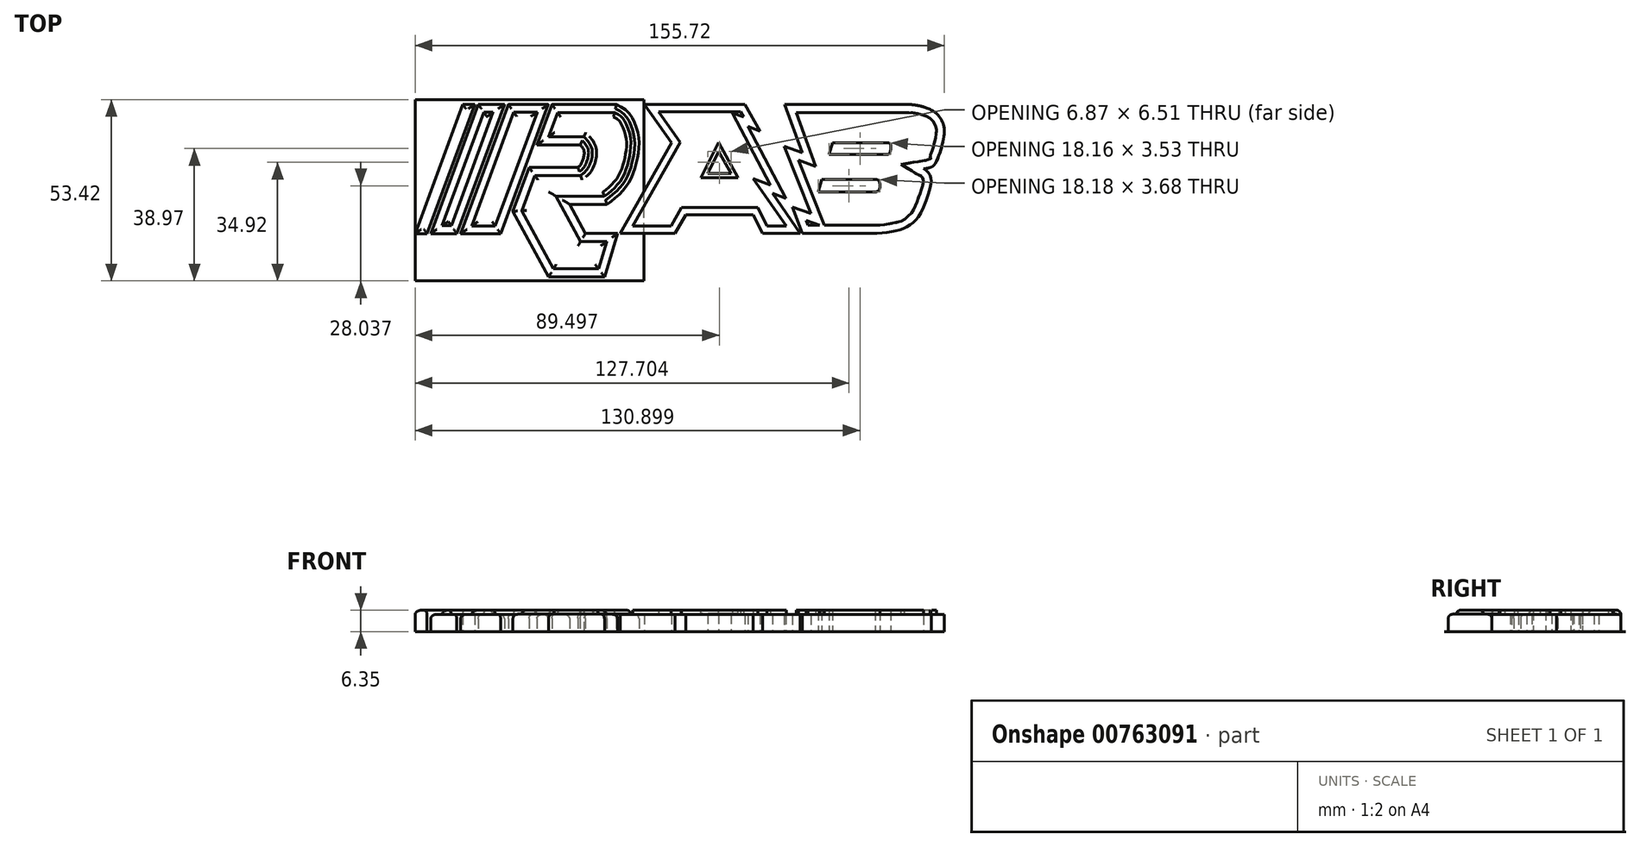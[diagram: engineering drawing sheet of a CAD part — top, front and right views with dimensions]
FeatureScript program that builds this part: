
annotation { "Feature Type Name" : "Feature", "Feature Type Description" : "" }
export const myFeature = defineFeature(function(context is Context, id is Id, definition is map)
    precondition{}
    {
        {
            var Q0;
            Q0=qCreatedBy(makeId("Top.planeOp"),FACE);
            var sketch = newSketch(context, id + "F0", { "sketchPlane" : qUnion([Q0])});
            skLineSegment(sketch, "E0", {"start": v(208.26, 38.07) * mm, "end": v(177.15, 38.07) * mm});
            skLineSegment(sketch, "E1", {"start": v(0, 0) * mm, "end": v(14, 38.07) * mm});
            skLineSegment(sketch, "E2", {"start": v(25.15, 0) * mm, "end": v(13.4, 0) * mm});
            skLineSegment(sketch, "E3", {"start": v(17.5, 38.07) * mm, "end": v(3.5, 0) * mm});
            skLineSegment(sketch, "E4", {"start": v(4.59, 0) * mm, "end": v(18.6, 38.07) * mm});
            skLineSegment(sketch, "E5", {"start": v(26.26, 38.07) * mm, "end": v(12.25, 0) * mm});
            skLineSegment(sketch, "E6", {"start": v(13.4, 0) * mm, "end": v(27.4, 38.07) * mm});
            skLineSegment(sketch, "E7", {"start": v(39.16, 38.07) * mm, "end": v(25.15, 0) * mm});
            skLineSegment(sketch, "E8", {"start": v(35.85, 26.18) * mm, "end": v(40.22, 38.07) * mm});
            skLineSegment(sketch, "E9", {"start": v(35.85, 26.18) * mm, "end": v(48.58, 26.18) * mm});
            skLineSegment(sketch, "E10", {"start": v(47.9, 19.52) * mm, "end": v(33.54, 19.52) * mm});
            skLineSegment(sketch, "E11", {"start": v(33.54, 19.52) * mm, "end": v(28.77, 6.57) * mm});
            skLineSegment(sketch, "E12", {"start": v(28.77, 6.57) * mm, "end": v(39.28, -12.73) * mm});
            skLineSegment(sketch, "E13", {"start": v(39.28, -12.73) * mm, "end": v(55.72, -12.73) * mm});
            skLineSegment(sketch, "E14", {"start": v(55.72, -12.73) * mm, "end": v(59.6, 0.09) * mm});
            skLineSegment(sketch, "E15", {"start": v(59.6, 0.09) * mm, "end": v(50.12, 0.09) * mm});
            skLineSegment(sketch, "E16", {"start": v(50.12, 0.09) * mm, "end": v(45.46, 8.65) * mm});
            skLineSegment(sketch, "E17", {"start": v(45.46, 8.65) * mm, "end": v(56.44, 8.65) * mm});
            skLineSegment(sketch, "E18", {"start": v(60.39, 0.09) * mm, "end": v(76.53, 0.09) * mm});
            skLineSegment(sketch, "E19", {"start": v(67.47, 38.07) * mm, "end": v(75.46, 26.74) * mm});
            skLineSegment(sketch, "E20", {"start": v(75.46, 26.74) * mm, "end": v(60.39, 0.09) * mm});
            skLineSegment(sketch, "E21", {"start": v(76.53, 0.09) * mm, "end": v(79.61, 5.54) * mm});
            skLineSegment(sketch, "E22", {"start": v(79.61, 5.54) * mm, "end": v(99.49, 5.54) * mm});
            skLineSegment(sketch, "E23", {"start": v(99.49, 5.54) * mm, "end": v(102.21, 0.09) * mm});
            skLineSegment(sketch, "E24", {"start": v(97.03, 38.07) * mm, "end": v(101.52, 30.22) * mm});
            skLineSegment(sketch, "E25", {"start": v(101.52, 30.22) * mm, "end": v(97.9, 31.58) * mm});
            skLineSegment(sketch, "E26", {"start": v(97.9, 31.58) * mm, "end": v(109.11, 10.42) * mm});
            skLineSegment(sketch, "E27", {"start": v(109.11, 10.42) * mm, "end": v(105.13, 11.87) * mm});
            skLineSegment(sketch, "E28", {"start": v(105.13, 11.87) * mm, "end": v(113.36, 0.09) * mm});
            skLineSegment(sketch, "E29", {"start": v(92.93, 17.75) * mm, "end": v(86.06, 17.75) * mm});
            skLineSegment(sketch, "E30", {"start": v(86.06, 17.75) * mm, "end": v(89.32, 24.25) * mm});
            skLineSegment(sketch, "E31", {"start": v(89.32, 24.25) * mm, "end": v(92.93, 17.75) * mm});
            skLineSegment(sketch, "E32", {"start": v(108.71, 38.07) * mm, "end": v(113.9, 23.8) * mm});
            skLineSegment(sketch, "E33", {"start": v(113.9, 23.8) * mm, "end": v(108.66, 25.8) * mm});
            skLineSegment(sketch, "E34", {"start": v(108.66, 25.8) * mm, "end": v(116.52, 5.9) * mm});
            skLineSegment(sketch, "E35", {"start": v(116.52, 5.9) * mm, "end": v(111, 7.9) * mm});
            skLineSegment(sketch, "E36", {"start": v(111, 7.9) * mm, "end": v(114, 0.09) * mm});
            skLineSegment(sketch, "E37", {"start": v(122.84, 26.81) * mm, "end": v(121.82, 23.29) * mm});
            skLineSegment(sketch, "E38", {"start": v(118.61, 12.28) * mm, "end": v(135.38, 12.28) * mm});
            skLineSegment(sketch, "E39", {"start": v(119.68, 15.96) * mm, "end": v(135.79, 15.96) * mm});
            skLineSegment(sketch, "E40", {"start": v(122.84, 26.81) * mm, "end": v(139.21, 26.81) * mm});
            skLineSegment(sketch, "E41", {"start": v(121.82, 23.29) * mm, "end": v(138.81, 23.29) * mm});
            skLineSegment(sketch, "E42", {"start": v(154.94, 38.07) * mm, "end": v(158.48, 30.05) * mm});
            skLineSegment(sketch, "E43", {"start": v(158.48, 30.05) * mm, "end": v(149.8, 0.09) * mm});
            skLineSegment(sketch, "E44", {"start": v(174.28, 38.07) * mm, "end": v(163.42, 0.09) * mm});
            skLineSegment(sketch, "E45", {"start": v(177.15, 38.07) * mm, "end": v(166.29, 0.09) * mm});
            skLineSegment(sketch, "E46", {"start": v(199.63, 25.83) * mm, "end": v(187.3, 25.83) * mm});
            skLineSegment(sketch, "E47", {"start": v(187.3, 25.83) * mm, "end": v(183.47, 12.44) * mm});
            skLineSegment(sketch, "E48", {"start": v(183.47, 12.44) * mm, "end": v(198.12, 12.44) * mm});
            skLineSegment(sketch, "E49", {"start": v(203.43, 21.85) * mm, "end": v(201.46, 14.99) * mm});
            skFitSpline(sketch, "E50", {"points": [v(219.55, 26.88) * mm, v(219.55, 31.52) * mm, v(217.56, 35.22) * mm, v(214.71, 36.84) * mm, v(208.26, 38.07) * mm], "startDerivative": vector(2.3, 18.78) * mm, "endDerivative": vector(-24.45, 0) * mm});
            skLineSegment(sketch, "E51", {"start": v(219.55, 26.88) * mm, "end": v(215.38, 11.32) * mm});
            skFitSpline(sketch, "E52", {"points": [v(149.65, 19.1) * mm, v(151.8, 19.57) * mm, v(153.28, 21.06) * mm, v(155.68, 29.22) * mm, v(155.1, 33.05) * mm, v(153.47, 35.33) * mm, v(150.12, 37.18) * mm, v(144.89, 38.07) * mm], "startDerivative": vector(20.2, 3.41) * mm, "endDerivative": vector(-28.09, 0) * mm});
            skFitSpline(sketch, "E53", {"points": [v(149.65, 19.1) * mm, v(151.02, 18) * mm, v(151.86, 16.02) * mm, v(151.72, 14.12) * mm, v(148.83, 6.08) * mm, v(146.58, 3.33) * mm, v(143.97, 1.57) * mm, v(140.72, 0.72) * mm, v(135.93, 0.09) * mm], "startDerivative": vector(16.43, -10.07) * mm, "endDerivative": vector(-33.98, 0) * mm});
            skFitSpline(sketch, "E54", {"points": [v(139.21, 26.81) * mm, v(139.63, 26.6) * mm, v(139.95, 26.07) * mm, v(139.77, 23.99) * mm, v(139.53, 23.54) * mm, v(138.81, 23.29) * mm], "startDerivative": vector(3.09, 0) * mm, "endDerivative": vector(-4.49, 0) * mm});
            skFitSpline(sketch, "E55", {"points": [v(135.79, 15.96) * mm, v(136.31, 15.73) * mm, v(136.7, 15.08) * mm, v(136.71, 13.28) * mm, v(136.38, 12.68) * mm, v(135.38, 12.28) * mm], "startDerivative": vector(3.73, 0) * mm, "endDerivative": vector(-8.7, -0.89) * mm});
            skFitSpline(sketch, "E56", {"points": [v(59.25, 38.07) * mm, v(62.12, 36.32) * mm, v(64.27, 33.3) * mm, v(65.78, 28.2) * mm, v(65.5, 22.76) * mm, v(63.84, 16.87) * mm, v(60.61, 12.07) * mm, v(56.44, 8.65) * mm], "startDerivative": vector(25.95, -13.02) * mm, "endDerivative": vector(-29.28, -21.25) * mm});
            skFitSpline(sketch, "E57", {"points": [v(199.63, 25.83) * mm, v(200.99, 25.52) * mm, v(202.05, 24.9) * mm, v(202.89, 23.96) * mm, v(203.43, 21.85) * mm], "startDerivative": vector(5.58, 0) * mm, "endDerivative": vector(-1.33, -10.82) * mm});
            skFitSpline(sketch, "E58", {"points": [v(198.12, 12.44) * mm, v(199.3, 12.72) * mm, v(200.4, 13.16) * mm, v(201.08, 13.97) * mm, v(201.46, 14.99) * mm], "startDerivative": vector(4.57, 1.01) * mm, "endDerivative": vector(1.33, 4.26) * mm});
            skLineSegment(sketch, "E59.trimOffspring", {"start": v(17.5, 38.07) * mm, "end": v(14, 38.07) * mm});
            skLineSegment(sketch, "E60.trimOffspring", {"start": v(26.26, 38.07) * mm, "end": v(18.6, 38.07) * mm});
            skLineSegment(sketch, "E61.trimOffspring", {"start": v(39.16, 38.07) * mm, "end": v(27.4, 38.07) * mm});
            skLineSegment(sketch, "E62.trimOffspring", {"start": v(59.25, 38.07) * mm, "end": v(40.22, 38.07) * mm});
            skLineSegment(sketch, "E63.trimOffspring", {"start": v(12.25, 0) * mm, "end": v(4.59, 0) * mm});
            skLineSegment(sketch, "E64.trimOffspring", {"start": v(3.5, 0) * mm, "end": v(0, 0) * mm});
            skLineSegment(sketch, "E65.trimOffspring", {"start": v(102.21, 0.09) * mm, "end": v(113.36, 0.09) * mm});
            skLineSegment(sketch, "E66.trimOffspring", {"start": v(114, 0.09) * mm, "end": v(135.93, 0.09) * mm});
            skLineSegment(sketch, "E67.trimOffspring", {"start": v(97.03, 38.07) * mm, "end": v(67.47, 38.07) * mm});
            skLineSegment(sketch, "E68.trimOffspring", {"start": v(119.68, 15.96) * mm, "end": v(118.61, 12.28) * mm});
            skLineSegment(sketch, "E69.trimOffspring", {"start": v(144.89, 38.07) * mm, "end": v(108.71, 38.07) * mm});
            skLineSegment(sketch, "E70.trimOffspring", {"start": v(149.8, 0.09) * mm, "end": v(163.42, 0.09) * mm});
            skLineSegment(sketch, "E71.trimOffspring", {"start": v(166.29, 0.09) * mm, "end": v(197.11, 0.09) * mm});
            skLineSegment(sketch, "E72.trimOffspring", {"start": v(174.28, 38.07) * mm, "end": v(154.94, 38.07) * mm});
            skFitSpline(sketch, "E73", {"points": [v(215.38, 11.32) * mm, v(214.17, 8.68) * mm, v(212.23, 5.94) * mm, v(209.39, 3.57) * mm, v(206.3, 1.9) * mm, v(202.66, 0.86) * mm, v(197.11, 0.09) * mm], "startDerivative": vector(-7.47, -18.05) * mm, "endDerivative": vector(-28.9, 0) * mm});
            skFitSpline(sketch, "E74", {"points": [v(48.58, 26.18) * mm, v(49.62, 24.65) * mm, v(49.56, 22.47) * mm, v(48.58, 20.18) * mm, v(47.9, 19.52) * mm], "startDerivative": vector(5.02, -5.67) * mm, "endDerivative": vector(-3.78, -2.78) * mm});
            skSolve(sketch);
        }
        {
            var Q0;
            Q0=makeQuery(id+"F0.imprint","IMPRINT",FACE,{"disambiguationData":[TD([[makeQuery(id+"F0.imprint","IMPRINT",EDGE,{"derivedFrom":sQuery(id+"F0.wireOp",EDGE,"E8")}),-1.0]])]});
            var Q1;
            Q1=makeQuery(id+"F0.imprint","IMPRINT",FACE,{"disambiguationData":[TD([[makeQuery(id+"F0.imprint","IMPRINT",EDGE,{"derivedFrom":sQuery(id+"F0.wireOp",EDGE,"E2")}),-1.0]])]});
            var Q2;
            Q2=makeQuery(id+"F0.imprint","IMPRINT",FACE,{"disambiguationData":[TD([[makeQuery(id+"F0.imprint","IMPRINT",EDGE,{"derivedFrom":sQuery(id+"F0.wireOp",EDGE,"E4")}),-1.0]])]});
            var Q3;
            Q3=makeQuery(id+"F0.imprint","IMPRINT",FACE,{"disambiguationData":[TD([[makeQuery(id+"F0.imprint","IMPRINT",EDGE,{"derivedFrom":sQuery(id+"F0.wireOp",EDGE,"E1")}),-1.0]])]});
            extrude(context, id + "F1", {"entities" : qUnion([Q0, Q1, Q2, Q3]), "depth" : 6.35 * mm, "offsetDistance" : 25.4 * mm});
        }
        {
            var Q0;
            Q0=qCreatedBy(makeId("Front.planeOp"),FACE);
            cPlane(context, id + "F2", {"entities" : qUnion([Q0]), "cplaneType" : CPlaneType.OFFSET, "offset" : 25.4 * mm, "oppositeDirection" : true, "width" : 152.4 * mm, "height" : 152.4 * mm});
        }
        {
            var Q0;
            Q0=qCreatedBy(id+"F2.planeOp",FACE);
            var sketch = newSketch(context, id + "F3", { "sketchPlane" : qUnion([Q0])});
            skLineSegment(sketch, "E75", {"start": v(63.44, 6.43) * mm, "end": v(63.44, 5.16) * mm});
            skLineSegment(sketch, "E76", {"start": v(63.44, 5.16) * mm, "end": v(65.98, 5.16) * mm});
            skLineSegment(sketch, "E77", {"start": v(65.98, 5.16) * mm, "end": v(65.98, 6.43) * mm});
            skLineSegment(sketch, "E78", {"start": v(65.98, 6.43) * mm, "end": v(63.44, 6.43) * mm});
            skSolve(sketch);
        }
        {
            var Q0;
            Q0=qSketchRegion(id+"F3",true);
            var Q1;
            Q1=makeQuery(id+"F1.opExtrude","CAP_EDGE",EDGE,{"disambiguationData":[OSD([sQuery(id+"F0.wireOp",EDGE,"E56")])],"isStart":false});
            var Q2;
            Q2=makeQuery(id+"F1.opExtrude","CAP_EDGE",EDGE,{"disambiguationData":[OSD([sQuery(id+"F0.wireOp",EDGE,"E17")])],"isStart":false});
            var Q3;
            Q3=makeQuery(id+"F1.opExtrude","CAP_EDGE",EDGE,{"disambiguationData":[OSD([sQuery(id+"F0.wireOp",EDGE,"E16")])],"isStart":false});
            var Q4;
            Q4=makeQuery(id+"F1.opExtrude","CAP_EDGE",EDGE,{"disambiguationData":[OSD([sQuery(id+"F0.wireOp",EDGE,"E15")])],"isStart":false});
            var Q5;
            Q5=makeQuery(id+"F1.opExtrude","CAP_EDGE",EDGE,{"disambiguationData":[OSD([sQuery(id+"F0.wireOp",EDGE,"E14")])],"isStart":false});
            var Q6;
            Q6=makeQuery(id+"F1.opExtrude","CAP_EDGE",EDGE,{"disambiguationData":[OSD([sQuery(id+"F0.wireOp",EDGE,"E13")])],"isStart":false});
            var Q7;
            Q7=makeQuery(id+"F1.opExtrude","CAP_EDGE",EDGE,{"disambiguationData":[OSD([sQuery(id+"F0.wireOp",EDGE,"E12")])],"isStart":false});
            var Q8;
            Q8=makeQuery(id+"F1.opExtrude","CAP_EDGE",EDGE,{"disambiguationData":[OSD([sQuery(id+"F0.wireOp",EDGE,"E11")])],"isStart":false});
            var Q9;
            Q9=makeQuery(id+"F1.opExtrude","CAP_EDGE",EDGE,{"disambiguationData":[OSD([sQuery(id+"F0.wireOp",EDGE,"E10")])],"isStart":false});
            var Q10;
            Q10=makeQuery(id+"F1.opExtrude","CAP_EDGE",EDGE,{"disambiguationData":[OSD([sQuery(id+"F0.wireOp",EDGE,"E74")])],"isStart":false});
            var Q11;
            Q11=makeQuery(id+"F1.opExtrude","CAP_EDGE",EDGE,{"disambiguationData":[OSD([sQuery(id+"F0.wireOp",EDGE,"E9")])],"isStart":false});
            var Q12;
            Q12=makeQuery(id+"F1.opExtrude","CAP_EDGE",EDGE,{"disambiguationData":[OSD([sQuery(id+"F0.wireOp",EDGE,"E8")])],"isStart":false});
            var Q13;
            Q13=makeQuery(id+"F1.opExtrude","CAP_EDGE",EDGE,{"disambiguationData":[OSD([sQuery(id+"F0.wireOp",EDGE,"E62.trimOffspring")])],"isStart":false});
            sweep(context, id + "F4", {"operationType" : NewBodyOperationType.REMOVE, "profiles" : qUnion([Q0]), "path" : qUnion([Q1, Q2, Q3, Q4, Q5, Q6, Q7, Q8, Q9, Q10, Q11, Q12, Q13])});
        }
        {
            var Q0;
            Q0=qCreatedBy(id+"F2.planeOp",FACE);
            var sketch = newSketch(context, id + "F5", { "sketchPlane" : qUnion([Q0])});
            skLineSegment(sketch, "E79", {"start": v(32.09, 6.42) * mm, "end": v(32.09, 5.16) * mm});
            skLineSegment(sketch, "E80", {"start": v(32.09, 5.16) * mm, "end": v(34.63, 5.16) * mm});
            skLineSegment(sketch, "E81", {"start": v(34.63, 5.16) * mm, "end": v(34.63, 6.42) * mm});
            skLineSegment(sketch, "E82", {"start": v(34.63, 6.42) * mm, "end": v(32.09, 6.42) * mm});
            skSolve(sketch);
        }
        {
            var Q0;
            Q0=qSketchRegion(id+"F5",true);
            var Q1;
            Q1=makeQuery(id+"F1.opExtrude","CAP_EDGE",EDGE,{"disambiguationData":[OSD([sQuery(id+"F0.wireOp",EDGE,"E7")])],"isStart":false});
            var Q2;
            Q2=makeQuery(id+"F1.opExtrude","CAP_EDGE",EDGE,{"disambiguationData":[OSD([sQuery(id+"F0.wireOp",EDGE,"E2")])],"isStart":false});
            var Q3;
            Q3=makeQuery(id+"F1.opExtrude","CAP_EDGE",EDGE,{"disambiguationData":[OSD([sQuery(id+"F0.wireOp",EDGE,"E6")])],"isStart":false});
            var Q4;
            Q4=makeQuery(id+"F1.opExtrude","CAP_EDGE",EDGE,{"disambiguationData":[OSD([sQuery(id+"F0.wireOp",EDGE,"E61.trimOffspring")])],"isStart":false});
            sweep(context, id + "F6", {"operationType" : NewBodyOperationType.REMOVE, "profiles" : qUnion([Q0]), "path" : qUnion([Q1, Q2, Q3, Q4])});
        }
        {
            var Q0;
            Q0=qCreatedBy(id+"F2.planeOp",FACE);
            var sketch = newSketch(context, id + "F7", { "sketchPlane" : qUnion([Q0])});
            skLineSegment(sketch, "E83", {"start": v(19.13, 6.42) * mm, "end": v(19.13, 5.16) * mm});
            skLineSegment(sketch, "E84", {"start": v(19.13, 5.16) * mm, "end": v(21.67, 5.16) * mm});
            skLineSegment(sketch, "E85", {"start": v(21.67, 5.16) * mm, "end": v(21.67, 6.42) * mm});
            skLineSegment(sketch, "E86", {"start": v(21.67, 6.42) * mm, "end": v(19.13, 6.42) * mm});
            skSolve(sketch);
        }
        {
            var Q0;
            Q0=qSketchRegion(id+"F7",true);
            var Q1;
            Q1=makeQuery(id+"F1.opExtrude","CAP_EDGE",EDGE,{"disambiguationData":[OSD([sQuery(id+"F0.wireOp",EDGE,"E5")])],"isStart":false});
            var Q2;
            Q2=makeQuery(id+"F1.opExtrude","CAP_EDGE",EDGE,{"disambiguationData":[OSD([sQuery(id+"F0.wireOp",EDGE,"E63.trimOffspring")])],"isStart":false});
            var Q3;
            Q3=makeQuery(id+"F1.opExtrude","CAP_EDGE",EDGE,{"disambiguationData":[OSD([sQuery(id+"F0.wireOp",EDGE,"E4")])],"isStart":false});
            var Q4;
            Q4=makeQuery(id+"F1.opExtrude","CAP_EDGE",EDGE,{"disambiguationData":[OSD([sQuery(id+"F0.wireOp",EDGE,"E60.trimOffspring")])],"isStart":false});
            sweep(context, id + "F8", {"operationType" : NewBodyOperationType.REMOVE, "profiles" : qUnion([Q0]), "path" : qUnion([Q1, Q2, Q3, Q4])});
        }
        {
            var Q0;
            {var subQ0=sQuery(id+"F0.wireOp",EDGE,"E56");Q0=makeQuery(id+"F4.boolean.opBoolean","INTERSECT",EDGE,{"derivedFrom":[makeQuery(id+"F1.opExtrude","CAP_FACE",FACE,{"disambiguationData":[OSD([sQuery(id+"F0.wireOp",EDGE,"E8"),sQuery(id+"F0.wireOp",EDGE,"E9"),sQuery(id+"F0.wireOp",EDGE,"E10"),sQuery(id+"F0.wireOp",EDGE,"E11"),sQuery(id+"F0.wireOp",EDGE,"E12"),sQuery(id+"F0.wireOp",EDGE,"E13"),sQuery(id+"F0.wireOp",EDGE,"E14"),sQuery(id+"F0.wireOp",EDGE,"E15"),sQuery(id+"F0.wireOp",EDGE,"E16"),sQuery(id+"F0.wireOp",EDGE,"E17"),subQ0,sQuery(id+"F0.wireOp",EDGE,"E62.trimOffspring"),sQuery(id+"F0.wireOp",EDGE,"E74")])],"isStart":false}),makeQuery(id+"F4.opSweep","SWEPT_FACE",FACE,{"disambiguationData":[OSD([subQ0,sQuery(id+"F3.wireOp",EDGE,"E75")])]})]});}
            var Q1;
            {var subQ0=sQuery(id+"F0.wireOp",EDGE,"E17");Q1=makeQuery(id+"F4.boolean.opBoolean","INTERSECT",EDGE,{"derivedFrom":[makeQuery(id+"F1.opExtrude","CAP_FACE",FACE,{"disambiguationData":[OSD([sQuery(id+"F0.wireOp",EDGE,"E8"),sQuery(id+"F0.wireOp",EDGE,"E9"),sQuery(id+"F0.wireOp",EDGE,"E10"),sQuery(id+"F0.wireOp",EDGE,"E11"),sQuery(id+"F0.wireOp",EDGE,"E12"),sQuery(id+"F0.wireOp",EDGE,"E13"),sQuery(id+"F0.wireOp",EDGE,"E14"),sQuery(id+"F0.wireOp",EDGE,"E15"),sQuery(id+"F0.wireOp",EDGE,"E16"),subQ0,sQuery(id+"F0.wireOp",EDGE,"E56"),sQuery(id+"F0.wireOp",EDGE,"E62.trimOffspring"),sQuery(id+"F0.wireOp",EDGE,"E74")])],"isStart":false}),makeQuery(id+"F4.opSweep","SWEPT_FACE",FACE,{"disambiguationData":[OSD([subQ0,sQuery(id+"F3.wireOp",EDGE,"E75")])]})]});}
            var Q2;
            {var subQ0=sQuery(id+"F0.wireOp",EDGE,"E16");Q2=makeQuery(id+"F4.boolean.opBoolean","INTERSECT",EDGE,{"derivedFrom":[makeQuery(id+"F1.opExtrude","CAP_FACE",FACE,{"disambiguationData":[OSD([sQuery(id+"F0.wireOp",EDGE,"E8"),sQuery(id+"F0.wireOp",EDGE,"E9"),sQuery(id+"F0.wireOp",EDGE,"E10"),sQuery(id+"F0.wireOp",EDGE,"E11"),sQuery(id+"F0.wireOp",EDGE,"E12"),sQuery(id+"F0.wireOp",EDGE,"E13"),sQuery(id+"F0.wireOp",EDGE,"E14"),sQuery(id+"F0.wireOp",EDGE,"E15"),subQ0,sQuery(id+"F0.wireOp",EDGE,"E17"),sQuery(id+"F0.wireOp",EDGE,"E56"),sQuery(id+"F0.wireOp",EDGE,"E62.trimOffspring"),sQuery(id+"F0.wireOp",EDGE,"E74")])],"isStart":false}),makeQuery(id+"F4.opSweep","SWEPT_FACE",FACE,{"disambiguationData":[OSD([subQ0,sQuery(id+"F3.wireOp",EDGE,"E75")])]})]});}
            var Q3;
            {var subQ0=sQuery(id+"F0.wireOp",EDGE,"E15");Q3=makeQuery(id+"F4.boolean.opBoolean","INTERSECT",EDGE,{"derivedFrom":[makeQuery(id+"F1.opExtrude","CAP_FACE",FACE,{"disambiguationData":[OSD([sQuery(id+"F0.wireOp",EDGE,"E8"),sQuery(id+"F0.wireOp",EDGE,"E9"),sQuery(id+"F0.wireOp",EDGE,"E10"),sQuery(id+"F0.wireOp",EDGE,"E11"),sQuery(id+"F0.wireOp",EDGE,"E12"),sQuery(id+"F0.wireOp",EDGE,"E13"),sQuery(id+"F0.wireOp",EDGE,"E14"),subQ0,sQuery(id+"F0.wireOp",EDGE,"E16"),sQuery(id+"F0.wireOp",EDGE,"E17"),sQuery(id+"F0.wireOp",EDGE,"E56"),sQuery(id+"F0.wireOp",EDGE,"E62.trimOffspring"),sQuery(id+"F0.wireOp",EDGE,"E74")])],"isStart":false}),makeQuery(id+"F4.opSweep","SWEPT_FACE",FACE,{"disambiguationData":[OSD([subQ0,sQuery(id+"F3.wireOp",EDGE,"E75")])]})]});}
            var Q4;
            {var subQ0=sQuery(id+"F0.wireOp",EDGE,"E14");Q4=makeQuery(id+"F4.boolean.opBoolean","INTERSECT",EDGE,{"derivedFrom":[makeQuery(id+"F1.opExtrude","CAP_FACE",FACE,{"disambiguationData":[OSD([sQuery(id+"F0.wireOp",EDGE,"E8"),sQuery(id+"F0.wireOp",EDGE,"E9"),sQuery(id+"F0.wireOp",EDGE,"E10"),sQuery(id+"F0.wireOp",EDGE,"E11"),sQuery(id+"F0.wireOp",EDGE,"E12"),sQuery(id+"F0.wireOp",EDGE,"E13"),subQ0,sQuery(id+"F0.wireOp",EDGE,"E15"),sQuery(id+"F0.wireOp",EDGE,"E16"),sQuery(id+"F0.wireOp",EDGE,"E17"),sQuery(id+"F0.wireOp",EDGE,"E56"),sQuery(id+"F0.wireOp",EDGE,"E62.trimOffspring"),sQuery(id+"F0.wireOp",EDGE,"E74")])],"isStart":false}),makeQuery(id+"F4.opSweep","SWEPT_FACE",FACE,{"disambiguationData":[OSD([subQ0,sQuery(id+"F3.wireOp",EDGE,"E75")])]})]});}
            var Q5;
            Q5=makeQuery(id+"F4.boolean.opBoolean","INTERSECT",EDGE,{"derivedFrom":[makeQuery(id+"F1.opExtrude","SWEPT_FACE",FACE,{"disambiguationData":[OSD([sQuery(id+"F0.wireOp",EDGE,"E13")])]}),makeQuery(id+"F4.opSweep","SWEPT_FACE",FACE,{"disambiguationData":[OSD([sQuery(id+"F0.wireOp",EDGE,"E17"),sQuery(id+"F3.wireOp",EDGE,"E76")])]})]});
            var Q6;
            Q6=makeQuery(id+"F4.boolean.opBoolean","INTERSECT",EDGE,{"derivedFrom":[makeQuery(id+"F1.opExtrude","SWEPT_FACE",FACE,{"disambiguationData":[OSD([sQuery(id+"F0.wireOp",EDGE,"E14")])]}),makeQuery(id+"F4.opSweep","SWEPT_FACE",FACE,{"disambiguationData":[OSD([sQuery(id+"F0.wireOp",EDGE,"E17"),sQuery(id+"F3.wireOp",EDGE,"E76")])]})]});
            var Q7;
            {var subQ0=sQuery(id+"F0.wireOp",EDGE,"E17");Q7=makeQuery(id+"F4.boolean.opBoolean","INTERSECT",EDGE,{"derivedFrom":[makeQuery(id+"F1.opExtrude","SWEPT_FACE",FACE,{"disambiguationData":[OSD([subQ0])]}),makeQuery(id+"F4.opSweep","SWEPT_FACE",FACE,{"disambiguationData":[OSD([subQ0,sQuery(id+"F3.wireOp",EDGE,"E76")])]})]});}
            var Q8;
            Q8=makeQuery(id+"F4.boolean.opBoolean","INTERSECT",EDGE,{"derivedFrom":[makeQuery(id+"F1.opExtrude","SWEPT_FACE",FACE,{"disambiguationData":[OSD([sQuery(id+"F0.wireOp",EDGE,"E16")])]}),makeQuery(id+"F4.opSweep","SWEPT_FACE",FACE,{"disambiguationData":[OSD([sQuery(id+"F0.wireOp",EDGE,"E17"),sQuery(id+"F3.wireOp",EDGE,"E76")])]})]});
            var Q9;
            Q9=makeQuery(id+"F4.boolean.opBoolean","INTERSECT",EDGE,{"derivedFrom":[makeQuery(id+"F1.opExtrude","SWEPT_FACE",FACE,{"disambiguationData":[OSD([sQuery(id+"F0.wireOp",EDGE,"E15")])]}),makeQuery(id+"F4.opSweep","SWEPT_FACE",FACE,{"disambiguationData":[OSD([sQuery(id+"F0.wireOp",EDGE,"E17"),sQuery(id+"F3.wireOp",EDGE,"E76")])]})]});
            var Q10;
            Q10=makeQuery(id+"F4.boolean.opBoolean","INTERSECT",EDGE,{"derivedFrom":[makeQuery(id+"F1.opExtrude","SWEPT_FACE",FACE,{"disambiguationData":[OSD([sQuery(id+"F0.wireOp",EDGE,"E56")])]}),makeQuery(id+"F4.opSweep","SWEPT_FACE",FACE,{"disambiguationData":[OSD([sQuery(id+"F0.wireOp",EDGE,"E17"),sQuery(id+"F3.wireOp",EDGE,"E76")])]})]});
            var Q11;
            {var subQ0=sQuery(id+"F0.wireOp",EDGE,"E13");Q11=makeQuery(id+"F4.boolean.opBoolean","INTERSECT",EDGE,{"derivedFrom":[makeQuery(id+"F1.opExtrude","CAP_FACE",FACE,{"disambiguationData":[OSD([sQuery(id+"F0.wireOp",EDGE,"E8"),sQuery(id+"F0.wireOp",EDGE,"E9"),sQuery(id+"F0.wireOp",EDGE,"E10"),sQuery(id+"F0.wireOp",EDGE,"E11"),sQuery(id+"F0.wireOp",EDGE,"E12"),subQ0,sQuery(id+"F0.wireOp",EDGE,"E14"),sQuery(id+"F0.wireOp",EDGE,"E15"),sQuery(id+"F0.wireOp",EDGE,"E16"),sQuery(id+"F0.wireOp",EDGE,"E17"),sQuery(id+"F0.wireOp",EDGE,"E56"),sQuery(id+"F0.wireOp",EDGE,"E62.trimOffspring"),sQuery(id+"F0.wireOp",EDGE,"E74")])],"isStart":false}),makeQuery(id+"F4.opSweep","SWEPT_FACE",FACE,{"disambiguationData":[OSD([subQ0,sQuery(id+"F3.wireOp",EDGE,"E75")])]})]});}
            var Q12;
            {var subQ0=sQuery(id+"F0.wireOp",EDGE,"E12");Q12=makeQuery(id+"F4.boolean.opBoolean","INTERSECT",EDGE,{"derivedFrom":[makeQuery(id+"F1.opExtrude","CAP_FACE",FACE,{"disambiguationData":[OSD([sQuery(id+"F0.wireOp",EDGE,"E8"),sQuery(id+"F0.wireOp",EDGE,"E9"),sQuery(id+"F0.wireOp",EDGE,"E10"),sQuery(id+"F0.wireOp",EDGE,"E11"),subQ0,sQuery(id+"F0.wireOp",EDGE,"E13"),sQuery(id+"F0.wireOp",EDGE,"E14"),sQuery(id+"F0.wireOp",EDGE,"E15"),sQuery(id+"F0.wireOp",EDGE,"E16"),sQuery(id+"F0.wireOp",EDGE,"E17"),sQuery(id+"F0.wireOp",EDGE,"E56"),sQuery(id+"F0.wireOp",EDGE,"E62.trimOffspring"),sQuery(id+"F0.wireOp",EDGE,"E74")])],"isStart":false}),makeQuery(id+"F4.opSweep","SWEPT_FACE",FACE,{"disambiguationData":[OSD([subQ0,sQuery(id+"F3.wireOp",EDGE,"E75")])]})]});}
            var Q13;
            Q13=makeQuery(id+"F4.boolean.opBoolean","INTERSECT",EDGE,{"derivedFrom":[makeQuery(id+"F1.opExtrude","SWEPT_FACE",FACE,{"disambiguationData":[OSD([sQuery(id+"F0.wireOp",EDGE,"E12")])]}),makeQuery(id+"F4.opSweep","SWEPT_FACE",FACE,{"disambiguationData":[OSD([sQuery(id+"F0.wireOp",EDGE,"E17"),sQuery(id+"F3.wireOp",EDGE,"E76")])]})]});
            var Q14;
            Q14=makeQuery(id+"F4.boolean.opBoolean","INTERSECT",EDGE,{"derivedFrom":[makeQuery(id+"F1.opExtrude","SWEPT_FACE",FACE,{"disambiguationData":[OSD([sQuery(id+"F0.wireOp",EDGE,"E11")])]}),makeQuery(id+"F4.opSweep","SWEPT_FACE",FACE,{"disambiguationData":[OSD([sQuery(id+"F0.wireOp",EDGE,"E17"),sQuery(id+"F3.wireOp",EDGE,"E76")])]})]});
            var Q15;
            Q15=makeQuery(id+"F4.boolean.opBoolean","INTERSECT",EDGE,{"derivedFrom":[makeQuery(id+"F1.opExtrude","SWEPT_FACE",FACE,{"disambiguationData":[OSD([sQuery(id+"F0.wireOp",EDGE,"E10")])]}),makeQuery(id+"F4.opSweep","SWEPT_FACE",FACE,{"disambiguationData":[OSD([sQuery(id+"F0.wireOp",EDGE,"E17"),sQuery(id+"F3.wireOp",EDGE,"E76")])]})]});
            var Q16;
            {var subQ0=sQuery(id+"F0.wireOp",EDGE,"E11");Q16=makeQuery(id+"F4.boolean.opBoolean","INTERSECT",EDGE,{"derivedFrom":[makeQuery(id+"F1.opExtrude","CAP_FACE",FACE,{"disambiguationData":[OSD([sQuery(id+"F0.wireOp",EDGE,"E8"),sQuery(id+"F0.wireOp",EDGE,"E9"),sQuery(id+"F0.wireOp",EDGE,"E10"),subQ0,sQuery(id+"F0.wireOp",EDGE,"E12"),sQuery(id+"F0.wireOp",EDGE,"E13"),sQuery(id+"F0.wireOp",EDGE,"E14"),sQuery(id+"F0.wireOp",EDGE,"E15"),sQuery(id+"F0.wireOp",EDGE,"E16"),sQuery(id+"F0.wireOp",EDGE,"E17"),sQuery(id+"F0.wireOp",EDGE,"E56"),sQuery(id+"F0.wireOp",EDGE,"E62.trimOffspring"),sQuery(id+"F0.wireOp",EDGE,"E74")])],"isStart":false}),makeQuery(id+"F4.opSweep","SWEPT_FACE",FACE,{"disambiguationData":[OSD([subQ0,sQuery(id+"F3.wireOp",EDGE,"E75")])]})]});}
            var Q17;
            {var subQ0=sQuery(id+"F0.wireOp",EDGE,"E10");Q17=makeQuery(id+"F4.boolean.opBoolean","INTERSECT",EDGE,{"derivedFrom":[makeQuery(id+"F1.opExtrude","CAP_FACE",FACE,{"disambiguationData":[OSD([sQuery(id+"F0.wireOp",EDGE,"E8"),sQuery(id+"F0.wireOp",EDGE,"E9"),subQ0,sQuery(id+"F0.wireOp",EDGE,"E11"),sQuery(id+"F0.wireOp",EDGE,"E12"),sQuery(id+"F0.wireOp",EDGE,"E13"),sQuery(id+"F0.wireOp",EDGE,"E14"),sQuery(id+"F0.wireOp",EDGE,"E15"),sQuery(id+"F0.wireOp",EDGE,"E16"),sQuery(id+"F0.wireOp",EDGE,"E17"),sQuery(id+"F0.wireOp",EDGE,"E56"),sQuery(id+"F0.wireOp",EDGE,"E62.trimOffspring"),sQuery(id+"F0.wireOp",EDGE,"E74")])],"isStart":false}),makeQuery(id+"F4.opSweep","SWEPT_FACE",FACE,{"disambiguationData":[OSD([subQ0,sQuery(id+"F3.wireOp",EDGE,"E75")])]})]});}
            var Q18;
            Q18=makeQuery(id+"F4.boolean.opBoolean","INTERSECT",EDGE,{"derivedFrom":[makeQuery(id+"F1.opExtrude","SWEPT_FACE",FACE,{"disambiguationData":[OSD([sQuery(id+"F0.wireOp",EDGE,"E74")])]}),makeQuery(id+"F4.opSweep","SWEPT_FACE",FACE,{"disambiguationData":[OSD([sQuery(id+"F0.wireOp",EDGE,"E17"),sQuery(id+"F3.wireOp",EDGE,"E76")])]})]});
            var Q19;
            {var subQ0=sQuery(id+"F0.wireOp",EDGE,"E74");Q19=makeQuery(id+"F4.boolean.opBoolean","INTERSECT",EDGE,{"derivedFrom":[makeQuery(id+"F1.opExtrude","CAP_FACE",FACE,{"disambiguationData":[OSD([sQuery(id+"F0.wireOp",EDGE,"E8"),sQuery(id+"F0.wireOp",EDGE,"E9"),sQuery(id+"F0.wireOp",EDGE,"E10"),sQuery(id+"F0.wireOp",EDGE,"E11"),sQuery(id+"F0.wireOp",EDGE,"E12"),sQuery(id+"F0.wireOp",EDGE,"E13"),sQuery(id+"F0.wireOp",EDGE,"E14"),sQuery(id+"F0.wireOp",EDGE,"E15"),sQuery(id+"F0.wireOp",EDGE,"E16"),sQuery(id+"F0.wireOp",EDGE,"E17"),sQuery(id+"F0.wireOp",EDGE,"E56"),sQuery(id+"F0.wireOp",EDGE,"E62.trimOffspring"),subQ0])],"isStart":false}),makeQuery(id+"F4.opSweep","SWEPT_FACE",FACE,{"disambiguationData":[OSD([subQ0,sQuery(id+"F3.wireOp",EDGE,"E75")])]})]});}
            var Q20;
            {var subQ0=sQuery(id+"F0.wireOp",EDGE,"E9");Q20=makeQuery(id+"F4.boolean.opBoolean","INTERSECT",EDGE,{"derivedFrom":[makeQuery(id+"F1.opExtrude","CAP_FACE",FACE,{"disambiguationData":[OSD([sQuery(id+"F0.wireOp",EDGE,"E8"),subQ0,sQuery(id+"F0.wireOp",EDGE,"E10"),sQuery(id+"F0.wireOp",EDGE,"E11"),sQuery(id+"F0.wireOp",EDGE,"E12"),sQuery(id+"F0.wireOp",EDGE,"E13"),sQuery(id+"F0.wireOp",EDGE,"E14"),sQuery(id+"F0.wireOp",EDGE,"E15"),sQuery(id+"F0.wireOp",EDGE,"E16"),sQuery(id+"F0.wireOp",EDGE,"E17"),sQuery(id+"F0.wireOp",EDGE,"E56"),sQuery(id+"F0.wireOp",EDGE,"E62.trimOffspring"),sQuery(id+"F0.wireOp",EDGE,"E74")])],"isStart":false}),makeQuery(id+"F4.opSweep","SWEPT_FACE",FACE,{"disambiguationData":[OSD([subQ0,sQuery(id+"F3.wireOp",EDGE,"E75")])]})]});}
            var Q21;
            Q21=makeQuery(id+"F4.boolean.opBoolean","INTERSECT",EDGE,{"derivedFrom":[makeQuery(id+"F1.opExtrude","SWEPT_FACE",FACE,{"disambiguationData":[OSD([sQuery(id+"F0.wireOp",EDGE,"E9")])]}),makeQuery(id+"F4.opSweep","SWEPT_FACE",FACE,{"disambiguationData":[OSD([sQuery(id+"F0.wireOp",EDGE,"E17"),sQuery(id+"F3.wireOp",EDGE,"E76")])]})]});
            var Q22;
            Q22=makeQuery(id+"F4.boolean.opBoolean","INTERSECT",EDGE,{"derivedFrom":[makeQuery(id+"F1.opExtrude","SWEPT_FACE",FACE,{"disambiguationData":[OSD([sQuery(id+"F0.wireOp",EDGE,"E8")])]}),makeQuery(id+"F4.opSweep","SWEPT_FACE",FACE,{"disambiguationData":[OSD([sQuery(id+"F0.wireOp",EDGE,"E17"),sQuery(id+"F3.wireOp",EDGE,"E76")])]})]});
            var Q23;
            {var subQ0=sQuery(id+"F0.wireOp",EDGE,"E62.trimOffspring");Q23=makeQuery(id+"F4.boolean.opBoolean","INTERSECT",EDGE,{"derivedFrom":[makeQuery(id+"F1.opExtrude","CAP_FACE",FACE,{"disambiguationData":[OSD([sQuery(id+"F0.wireOp",EDGE,"E8"),sQuery(id+"F0.wireOp",EDGE,"E9"),sQuery(id+"F0.wireOp",EDGE,"E10"),sQuery(id+"F0.wireOp",EDGE,"E11"),sQuery(id+"F0.wireOp",EDGE,"E12"),sQuery(id+"F0.wireOp",EDGE,"E13"),sQuery(id+"F0.wireOp",EDGE,"E14"),sQuery(id+"F0.wireOp",EDGE,"E15"),sQuery(id+"F0.wireOp",EDGE,"E16"),sQuery(id+"F0.wireOp",EDGE,"E17"),sQuery(id+"F0.wireOp",EDGE,"E56"),subQ0,sQuery(id+"F0.wireOp",EDGE,"E74")])],"isStart":false}),makeQuery(id+"F4.opSweep","SWEPT_FACE",FACE,{"disambiguationData":[OSD([subQ0,sQuery(id+"F3.wireOp",EDGE,"E75")])]})]});}
            var Q24;
            {var subQ0=sQuery(id+"F0.wireOp",EDGE,"E8");Q24=makeQuery(id+"F4.boolean.opBoolean","INTERSECT",EDGE,{"derivedFrom":[makeQuery(id+"F1.opExtrude","CAP_FACE",FACE,{"disambiguationData":[OSD([subQ0,sQuery(id+"F0.wireOp",EDGE,"E9"),sQuery(id+"F0.wireOp",EDGE,"E10"),sQuery(id+"F0.wireOp",EDGE,"E11"),sQuery(id+"F0.wireOp",EDGE,"E12"),sQuery(id+"F0.wireOp",EDGE,"E13"),sQuery(id+"F0.wireOp",EDGE,"E14"),sQuery(id+"F0.wireOp",EDGE,"E15"),sQuery(id+"F0.wireOp",EDGE,"E16"),sQuery(id+"F0.wireOp",EDGE,"E17"),sQuery(id+"F0.wireOp",EDGE,"E56"),sQuery(id+"F0.wireOp",EDGE,"E62.trimOffspring"),sQuery(id+"F0.wireOp",EDGE,"E74")])],"isStart":false}),makeQuery(id+"F4.opSweep","SWEPT_FACE",FACE,{"disambiguationData":[OSD([subQ0,sQuery(id+"F3.wireOp",EDGE,"E75")])]})]});}
            var Q25;
            Q25=makeQuery(id+"F4.boolean.opBoolean","INTERSECT",EDGE,{"derivedFrom":[makeQuery(id+"F1.opExtrude","SWEPT_FACE",FACE,{"disambiguationData":[OSD([sQuery(id+"F0.wireOp",EDGE,"E62.trimOffspring")])]}),makeQuery(id+"F4.opSweep","SWEPT_FACE",FACE,{"disambiguationData":[OSD([sQuery(id+"F0.wireOp",EDGE,"E17"),sQuery(id+"F3.wireOp",EDGE,"E76")])]})]});
            var Q26;
            {var subQ0=sQuery(id+"F0.wireOp",EDGE,"E7");Q26=makeQuery(id+"F6.boolean.opBoolean","INTERSECT",EDGE,{"derivedFrom":[makeQuery(id+"F1.opExtrude","CAP_FACE",FACE,{"disambiguationData":[OSD([sQuery(id+"F0.wireOp",EDGE,"E2"),sQuery(id+"F0.wireOp",EDGE,"E6"),subQ0,sQuery(id+"F0.wireOp",EDGE,"E61.trimOffspring")])],"isStart":false}),makeQuery(id+"F6.opSweep","SWEPT_FACE",FACE,{"disambiguationData":[OSD([subQ0,sQuery(id+"F5.wireOp",EDGE,"E79")])]})]});}
            var Q27;
            {var subQ0=sQuery(id+"F0.wireOp",EDGE,"E2");Q27=makeQuery(id+"F6.boolean.opBoolean","INTERSECT",EDGE,{"derivedFrom":[makeQuery(id+"F1.opExtrude","CAP_FACE",FACE,{"disambiguationData":[OSD([subQ0,sQuery(id+"F0.wireOp",EDGE,"E6"),sQuery(id+"F0.wireOp",EDGE,"E7"),sQuery(id+"F0.wireOp",EDGE,"E61.trimOffspring")])],"isStart":false}),makeQuery(id+"F6.opSweep","SWEPT_FACE",FACE,{"disambiguationData":[OSD([subQ0,sQuery(id+"F5.wireOp",EDGE,"E79")])]})]});}
            var Q28;
            {var subQ0=sQuery(id+"F0.wireOp",EDGE,"E6");Q28=makeQuery(id+"F6.boolean.opBoolean","INTERSECT",EDGE,{"derivedFrom":[makeQuery(id+"F1.opExtrude","CAP_FACE",FACE,{"disambiguationData":[OSD([sQuery(id+"F0.wireOp",EDGE,"E2"),subQ0,sQuery(id+"F0.wireOp",EDGE,"E7"),sQuery(id+"F0.wireOp",EDGE,"E61.trimOffspring")])],"isStart":false}),makeQuery(id+"F6.opSweep","SWEPT_FACE",FACE,{"disambiguationData":[OSD([subQ0,sQuery(id+"F5.wireOp",EDGE,"E79")])]})]});}
            var Q29;
            {var subQ0=sQuery(id+"F0.wireOp",EDGE,"E61.trimOffspring");Q29=makeQuery(id+"F6.boolean.opBoolean","INTERSECT",EDGE,{"derivedFrom":[makeQuery(id+"F1.opExtrude","CAP_FACE",FACE,{"disambiguationData":[OSD([sQuery(id+"F0.wireOp",EDGE,"E2"),sQuery(id+"F0.wireOp",EDGE,"E6"),sQuery(id+"F0.wireOp",EDGE,"E7"),subQ0])],"isStart":false}),makeQuery(id+"F6.opSweep","SWEPT_FACE",FACE,{"disambiguationData":[OSD([subQ0,sQuery(id+"F5.wireOp",EDGE,"E79")])]})]});}
            var Q30;
            Q30=makeQuery(id+"F6.boolean.opBoolean","INTERSECT",EDGE,{"derivedFrom":[makeQuery(id+"F1.opExtrude","SWEPT_FACE",FACE,{"disambiguationData":[OSD([sQuery(id+"F0.wireOp",EDGE,"E61.trimOffspring")])]}),makeQuery(id+"F6.opSweep","SWEPT_FACE",FACE,{"disambiguationData":[OSD([sQuery(id+"F0.wireOp",EDGE,"E2"),sQuery(id+"F5.wireOp",EDGE,"E80")])]})]});
            var Q31;
            Q31=makeQuery(id+"F6.boolean.opBoolean","INTERSECT",EDGE,{"derivedFrom":[makeQuery(id+"F1.opExtrude","SWEPT_FACE",FACE,{"disambiguationData":[OSD([sQuery(id+"F0.wireOp",EDGE,"E7")])]}),makeQuery(id+"F6.opSweep","SWEPT_FACE",FACE,{"disambiguationData":[OSD([sQuery(id+"F0.wireOp",EDGE,"E2"),sQuery(id+"F5.wireOp",EDGE,"E80")])]})]});
            var Q32;
            Q32=makeQuery(id+"F6.boolean.opBoolean","INTERSECT",EDGE,{"derivedFrom":[makeQuery(id+"F1.opExtrude","SWEPT_FACE",FACE,{"disambiguationData":[OSD([sQuery(id+"F0.wireOp",EDGE,"E6")])]}),makeQuery(id+"F6.opSweep","SWEPT_FACE",FACE,{"disambiguationData":[OSD([sQuery(id+"F0.wireOp",EDGE,"E2"),sQuery(id+"F5.wireOp",EDGE,"E80")])]})]});
            var Q33;
            {var subQ0=sQuery(id+"F0.wireOp",EDGE,"E2");Q33=makeQuery(id+"F6.boolean.opBoolean","INTERSECT",EDGE,{"derivedFrom":[makeQuery(id+"F1.opExtrude","SWEPT_FACE",FACE,{"disambiguationData":[OSD([subQ0])]}),makeQuery(id+"F6.opSweep","SWEPT_FACE",FACE,{"disambiguationData":[OSD([subQ0,sQuery(id+"F5.wireOp",EDGE,"E80")])]})]});}
            var Q34;
            {var subQ0=sQuery(id+"F0.wireOp",EDGE,"E5");Q34=makeQuery(id+"F8.boolean.opBoolean","INTERSECT",EDGE,{"derivedFrom":[makeQuery(id+"F1.opExtrude","CAP_FACE",FACE,{"disambiguationData":[OSD([sQuery(id+"F0.wireOp",EDGE,"E4"),subQ0,sQuery(id+"F0.wireOp",EDGE,"E60.trimOffspring"),sQuery(id+"F0.wireOp",EDGE,"E63.trimOffspring")])],"isStart":false}),makeQuery(id+"F8.opSweep","SWEPT_FACE",FACE,{"disambiguationData":[OSD([subQ0,sQuery(id+"F7.wireOp",EDGE,"E83")])]})]});}
            var Q35;
            Q35=makeQuery(id+"F8.boolean.opBoolean","INTERSECT",EDGE,{"derivedFrom":[makeQuery(id+"F1.opExtrude","SWEPT_FACE",FACE,{"disambiguationData":[OSD([sQuery(id+"F0.wireOp",EDGE,"E5")])]}),makeQuery(id+"F8.opSweep","SWEPT_FACE",FACE,{"disambiguationData":[OSD([sQuery(id+"F0.wireOp",EDGE,"E63.trimOffspring"),sQuery(id+"F7.wireOp",EDGE,"E84")])]})]});
            var Q36;
            {var subQ0=sQuery(id+"F0.wireOp",EDGE,"E63.trimOffspring");Q36=makeQuery(id+"F8.boolean.opBoolean","INTERSECT",EDGE,{"derivedFrom":[makeQuery(id+"F1.opExtrude","CAP_FACE",FACE,{"disambiguationData":[OSD([sQuery(id+"F0.wireOp",EDGE,"E4"),sQuery(id+"F0.wireOp",EDGE,"E5"),sQuery(id+"F0.wireOp",EDGE,"E60.trimOffspring"),subQ0])],"isStart":false}),makeQuery(id+"F8.opSweep","SWEPT_FACE",FACE,{"disambiguationData":[OSD([subQ0,sQuery(id+"F7.wireOp",EDGE,"E83")])]})]});}
            var Q37;
            {var subQ0=sQuery(id+"F0.wireOp",EDGE,"E63.trimOffspring");Q37=makeQuery(id+"F8.boolean.opBoolean","INTERSECT",EDGE,{"derivedFrom":[makeQuery(id+"F1.opExtrude","SWEPT_FACE",FACE,{"disambiguationData":[OSD([subQ0])]}),makeQuery(id+"F8.opSweep","SWEPT_FACE",FACE,{"disambiguationData":[OSD([subQ0,sQuery(id+"F7.wireOp",EDGE,"E84")])]})]});}
            var Q38;
            {var subQ0=sQuery(id+"F0.wireOp",EDGE,"E4");Q38=makeQuery(id+"F8.boolean.opBoolean","INTERSECT",EDGE,{"derivedFrom":[makeQuery(id+"F1.opExtrude","CAP_FACE",FACE,{"disambiguationData":[OSD([subQ0,sQuery(id+"F0.wireOp",EDGE,"E5"),sQuery(id+"F0.wireOp",EDGE,"E60.trimOffspring"),sQuery(id+"F0.wireOp",EDGE,"E63.trimOffspring")])],"isStart":false}),makeQuery(id+"F8.opSweep","SWEPT_FACE",FACE,{"disambiguationData":[OSD([subQ0,sQuery(id+"F7.wireOp",EDGE,"E83")])]})]});}
            var Q39;
            Q39=makeQuery(id+"F8.boolean.opBoolean","INTERSECT",EDGE,{"derivedFrom":[makeQuery(id+"F1.opExtrude","SWEPT_FACE",FACE,{"disambiguationData":[OSD([sQuery(id+"F0.wireOp",EDGE,"E4")])]}),makeQuery(id+"F8.opSweep","SWEPT_FACE",FACE,{"disambiguationData":[OSD([sQuery(id+"F0.wireOp",EDGE,"E63.trimOffspring"),sQuery(id+"F7.wireOp",EDGE,"E84")])]})]});
            var Q40;
            Q40=makeQuery(id+"F1.opExtrude","CAP_FACE",FACE,{"disambiguationData":[OSD([sQuery(id+"F0.wireOp",EDGE,"E4"),sQuery(id+"F0.wireOp",EDGE,"E5"),sQuery(id+"F0.wireOp",EDGE,"E60.trimOffspring"),sQuery(id+"F0.wireOp",EDGE,"E63.trimOffspring")])],"isStart":false});
            var Q41;
            Q41=makeQuery(id+"F8.boolean.opBoolean","INTERSECT",EDGE,{"derivedFrom":[makeQuery(id+"F1.opExtrude","SWEPT_FACE",FACE,{"disambiguationData":[OSD([sQuery(id+"F0.wireOp",EDGE,"E60.trimOffspring")])]}),makeQuery(id+"F8.opSweep","SWEPT_FACE",FACE,{"disambiguationData":[OSD([sQuery(id+"F0.wireOp",EDGE,"E63.trimOffspring"),sQuery(id+"F7.wireOp",EDGE,"E84")])]})]});
            var Q42;
            Q42=makeQuery(id+"F1.opExtrude","CAP_EDGE",EDGE,{"disambiguationData":[OSD([sQuery(id+"F0.wireOp",EDGE,"E3")])],"isStart":false});
            var Q43;
            Q43=makeQuery(id+"F1.opExtrude","CAP_EDGE",EDGE,{"disambiguationData":[OSD([sQuery(id+"F0.wireOp",EDGE,"E59.trimOffspring")])],"isStart":false});
            var Q44;
            Q44=makeQuery(id+"F1.opExtrude","CAP_EDGE",EDGE,{"disambiguationData":[OSD([sQuery(id+"F0.wireOp",EDGE,"E1")])],"isStart":false});
            var Q45;
            Q45=makeQuery(id+"F1.opExtrude","CAP_EDGE",EDGE,{"disambiguationData":[OSD([sQuery(id+"F0.wireOp",EDGE,"E64.trimOffspring")])],"isStart":false});
            fillet(context, id + "F9", {"entities" : qUnion([Q0, Q1, Q2, Q3, Q4, Q5, Q6, Q7, Q8, Q9, Q10, Q11, Q12, Q13, Q14, Q15, Q16, Q17, Q18, Q19, Q20, Q21, Q22, Q23, Q24, Q25, Q26, Q27, Q28, Q29, Q30, Q31, Q32, Q33, Q34, Q35, Q36, Q37, Q38, Q39, Q40, Q41, Q42, Q43, Q44, Q45]), "radius" : 1.27 * mm, "tangentPropagation" : true, "allowEdgeOverflow" : false});
        }
        {
            var Q0;
            Q0=qCreatedBy(makeId("Top.planeOp"),FACE);
            var sketch = newSketch(context, id + "F10", { "sketchPlane" : qUnion([Q0])});
            skLineSegment(sketch, "E87.bottom", {"start": v(0, -13.92) * mm, "end": v(67.33, -13.92) * mm});
            skLineSegment(sketch, "E87.top", {"start": v(0, 39.5) * mm, "end": v(67.33, 39.5) * mm});
            skLineSegment(sketch, "E87.left", {"start": v(0, -13.92) * mm, "end": v(0, 39.5) * mm});
            skLineSegment(sketch, "E87.right", {"start": v(67.33, -13.92) * mm, "end": v(67.33, 39.5) * mm});
            skSolve(sketch);
        }
        {
            var Q0;
            Q0=qSketchRegion(id+"F10",true);
            extrude(context, id + "F11", {"entities" : qUnion([Q0]), "depth" : 0 * mm, "offsetDistance" : 25.4 * mm});
        }
        {
            var Q0;
            Q0=makeQuery(id+"F0.imprint","IMPRINT",FACE,{"disambiguationData":[TD([[makeQuery(id+"F0.imprint","IMPRINT",EDGE,{"derivedFrom":sQuery(id+"F0.wireOp",EDGE,"E18")}),1.0]])]});
            var Q1;
            Q1=makeQuery(id+"F0.imprint","IMPRINT",FACE,{"disambiguationData":[TD([[makeQuery(id+"F0.imprint","IMPRINT",EDGE,{"derivedFrom":sQuery(id+"F0.wireOp",EDGE,"E32")}),1.0]])]});
            extrude(context, id + "F12", {"entities" : qUnion([Q0, Q1]), "depth" : 6.35 * mm, "offsetDistance" : 25.4 * mm});
        }
        {
            var Q0;
            Q0=qCreatedBy(id+"F2.planeOp",FACE);
            var sketch = newSketch(context, id + "F13", { "sketchPlane" : qUnion([Q0])});
            skLineSegment(sketch, "E88", {"start": v(74.64, 6.39) * mm, "end": v(74.64, 5.12) * mm});
            skLineSegment(sketch, "E89", {"start": v(74.64, 5.12) * mm, "end": v(77.18, 5.12) * mm});
            skLineSegment(sketch, "E90", {"start": v(77.18, 5.12) * mm, "end": v(77.18, 6.39) * mm});
            skLineSegment(sketch, "E91", {"start": v(77.18, 6.39) * mm, "end": v(74.64, 6.39) * mm});
            skSolve(sketch);
        }
        {
            var Q0;
            Q0=qSketchRegion(id+"F13",true);
            var Q1;
            Q1=makeQuery(id+"F12.opExtrude","CAP_EDGE",EDGE,{"disambiguationData":[OSD([sQuery(id+"F0.wireOp",EDGE,"E20")])],"isStart":false});
            var Q2;
            Q2=makeQuery(id+"F12.opExtrude","CAP_EDGE",EDGE,{"disambiguationData":[OSD([sQuery(id+"F0.wireOp",EDGE,"E19")])],"isStart":false});
            var Q3;
            Q3=makeQuery(id+"F12.opExtrude","CAP_EDGE",EDGE,{"disambiguationData":[OSD([sQuery(id+"F0.wireOp",EDGE,"E18")])],"isStart":false});
            var Q4;
            Q4=makeQuery(id+"F12.opExtrude","CAP_EDGE",EDGE,{"disambiguationData":[OSD([sQuery(id+"F0.wireOp",EDGE,"E21")])],"isStart":false});
            var Q5;
            Q5=makeQuery(id+"F12.opExtrude","CAP_EDGE",EDGE,{"disambiguationData":[OSD([sQuery(id+"F0.wireOp",EDGE,"E22")])],"isStart":false});
            var Q6;
            Q6=makeQuery(id+"F12.opExtrude","CAP_EDGE",EDGE,{"disambiguationData":[OSD([sQuery(id+"F0.wireOp",EDGE,"E23")])],"isStart":false});
            var Q7;
            Q7=makeQuery(id+"F12.opExtrude","CAP_EDGE",EDGE,{"disambiguationData":[OSD([sQuery(id+"F0.wireOp",EDGE,"E65.trimOffspring")])],"isStart":false});
            var Q8;
            Q8=makeQuery(id+"F12.opExtrude","CAP_EDGE",EDGE,{"disambiguationData":[OSD([sQuery(id+"F0.wireOp",EDGE,"E28")])],"isStart":false});
            var Q9;
            Q9=makeQuery(id+"F12.opExtrude","CAP_EDGE",EDGE,{"disambiguationData":[OSD([sQuery(id+"F0.wireOp",EDGE,"E27")])],"isStart":false});
            var Q10;
            Q10=makeQuery(id+"F12.opExtrude","CAP_EDGE",EDGE,{"disambiguationData":[OSD([sQuery(id+"F0.wireOp",EDGE,"E26")])],"isStart":false});
            var Q11;
            Q11=makeQuery(id+"F12.opExtrude","CAP_EDGE",EDGE,{"disambiguationData":[OSD([sQuery(id+"F0.wireOp",EDGE,"E25")])],"isStart":false});
            var Q12;
            Q12=makeQuery(id+"F12.opExtrude","CAP_EDGE",EDGE,{"disambiguationData":[OSD([sQuery(id+"F0.wireOp",EDGE,"E24")])],"isStart":false});
            var Q13;
            Q13=makeQuery(id+"F12.opExtrude","CAP_EDGE",EDGE,{"disambiguationData":[OSD([sQuery(id+"F0.wireOp",EDGE,"E67.trimOffspring")])],"isStart":false});
            sweep(context, id + "F14", {"operationType" : NewBodyOperationType.REMOVE, "profiles" : qUnion([Q0]), "path" : qUnion([Q1, Q2, Q3, Q4, Q5, Q6, Q7, Q8, Q9, Q10, Q11, Q12, Q13])});
        }
        {
            var Q0;
            Q0=qCreatedBy(id+"F2.planeOp",FACE);
            var sketch = newSketch(context, id + "F15", { "sketchPlane" : qUnion([Q0])});
            skLineSegment(sketch, "E92", {"start": v(88.5, 6.6) * mm, "end": v(88.5, 5.33) * mm});
            skLineSegment(sketch, "E93", {"start": v(88.5, 5.33) * mm, "end": v(91.04, 5.33) * mm});
            skLineSegment(sketch, "E94", {"start": v(91.04, 5.33) * mm, "end": v(91.04, 6.6) * mm});
            skLineSegment(sketch, "E95", {"start": v(91.04, 6.6) * mm, "end": v(88.5, 6.6) * mm});
            skSolve(sketch);
        }
        {
            var Q0;
            Q0=qSketchRegion(id+"F15",true);
            var Q1;
            Q1=makeQuery(id+"F12.opExtrude","CAP_EDGE",EDGE,{"disambiguationData":[OSD([sQuery(id+"F0.wireOp",EDGE,"E31")])],"isStart":false});
            var Q2;
            Q2=makeQuery(id+"F12.opExtrude","CAP_EDGE",EDGE,{"disambiguationData":[OSD([sQuery(id+"F0.wireOp",EDGE,"E29")])],"isStart":false});
            var Q3;
            Q3=makeQuery(id+"F12.opExtrude","CAP_EDGE",EDGE,{"disambiguationData":[OSD([sQuery(id+"F0.wireOp",EDGE,"E30")])],"isStart":false});
            sweep(context, id + "F16", {"operationType" : NewBodyOperationType.REMOVE, "profiles" : qUnion([Q0]), "path" : qUnion([Q1, Q2, Q3])});
        }
        {
            var Q0;
            Q0=qCreatedBy(id+"F2.planeOp",FACE);
            var sketch = newSketch(context, id + "F17", { "sketchPlane" : qUnion([Q0])});
            skLineSegment(sketch, "E96", {"start": v(113.3, 6.36) * mm, "end": v(113.3, 5.1) * mm});
            skLineSegment(sketch, "E97", {"start": v(113.3, 5.1) * mm, "end": v(115.85, 5.1) * mm});
            skLineSegment(sketch, "E98", {"start": v(115.85, 5.1) * mm, "end": v(115.85, 6.36) * mm});
            skLineSegment(sketch, "E99", {"start": v(115.85, 6.36) * mm, "end": v(113.3, 6.36) * mm});
            skSolve(sketch);
        }
        {
            var Q0;
            Q0=qSketchRegion(id+"F17",true);
            var Q1;
            Q1=qConstructionFilter(qBodyType(qCreatedBy(id+"F17",EDGE),BodyType.WIRE),ConstructionObject.NO);
            var Q2;
            Q2=makeQuery(id+"F12.opExtrude","CAP_EDGE",EDGE,{"disambiguationData":[OSD([sQuery(id+"F0.wireOp",EDGE,"E32")])],"isStart":false});
            var Q3;
            Q3=makeQuery(id+"F12.opExtrude","CAP_EDGE",EDGE,{"disambiguationData":[OSD([sQuery(id+"F0.wireOp",EDGE,"E33")])],"isStart":false});
            var Q4;
            Q4=makeQuery(id+"F12.opExtrude","CAP_EDGE",EDGE,{"disambiguationData":[OSD([sQuery(id+"F0.wireOp",EDGE,"E34")])],"isStart":false});
            var Q5;
            Q5=makeQuery(id+"F12.opExtrude","CAP_EDGE",EDGE,{"disambiguationData":[OSD([sQuery(id+"F0.wireOp",EDGE,"E35")])],"isStart":false});
            var Q6;
            Q6=makeQuery(id+"F12.opExtrude","CAP_EDGE",EDGE,{"disambiguationData":[OSD([sQuery(id+"F0.wireOp",EDGE,"E36")])],"isStart":false});
            var Q7;
            Q7=makeQuery(id+"F12.opExtrude","CAP_EDGE",EDGE,{"disambiguationData":[OSD([sQuery(id+"F0.wireOp",EDGE,"E66.trimOffspring")])],"isStart":false});
            var Q8;
            Q8=makeQuery(id+"F12.opExtrude","CAP_EDGE",EDGE,{"disambiguationData":[OSD([sQuery(id+"F0.wireOp",EDGE,"E69.trimOffspring")])],"isStart":false});
            var Q9;
            Q9=makeQuery(id+"F12.opExtrude","CAP_EDGE",EDGE,{"disambiguationData":[OSD([sQuery(id+"F0.wireOp",EDGE,"E52")])],"isStart":false});
            var Q10;
            Q10=makeQuery(id+"F12.opExtrude","CAP_EDGE",EDGE,{"disambiguationData":[OSD([sQuery(id+"F0.wireOp",EDGE,"E53")])],"isStart":false});
            sweep(context, id + "F18", {"operationType" : NewBodyOperationType.REMOVE, "profiles" : qUnion([Q0]), "surfaceProfiles" : qUnion([Q1]), "path" : qUnion([Q2, Q3, Q4, Q5, Q6, Q7, Q8, Q9, Q10])});
        }
    });
